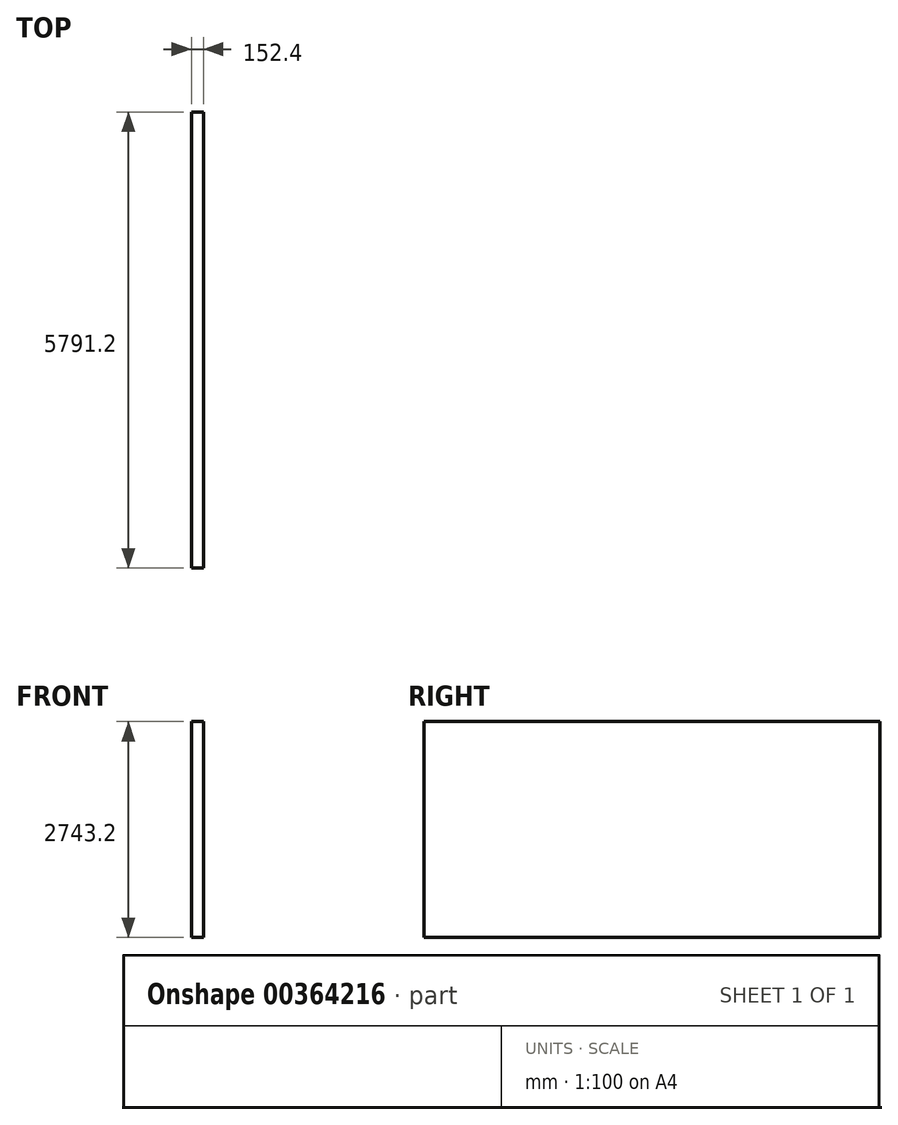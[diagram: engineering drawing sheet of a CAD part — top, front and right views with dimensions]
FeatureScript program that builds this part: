
annotation { "Feature Type Name" : "Feature", "Feature Type Description" : "" }
export const myFeature = defineFeature(function(context is Context, id is Id, definition is map)
    precondition{}
    {
        {
            var Q0;
            Q0=qCreatedBy(makeId("Top.planeOp"),FACE);
            var sketch = newSketch(context, id + "F0", { "sketchPlane" : qUnion([Q0])});
            skLineSegment(sketch, "E0.bottom", {"start": v(0, 0) * mm, "end": v(152.4, 0) * mm});
            skLineSegment(sketch, "E0.top", {"start": v(0, 5791.2) * mm, "end": v(152.4, 5791.2) * mm});
            skLineSegment(sketch, "E0.left", {"start": v(0, 0) * mm, "end": v(0, 5791.2) * mm});
            skLineSegment(sketch, "E0.right", {"start": v(152.4, 0) * mm, "end": v(152.4, 5791.2) * mm});
            skSolve(sketch);
        }
        {
            var Q0;
            Q0 = qSketchRegion(id + "F0", true);
            extrude(context, id + "F1", {"entities" : qUnion([Q0]), "depth" : 2743.2 * mm});
        }
    });
